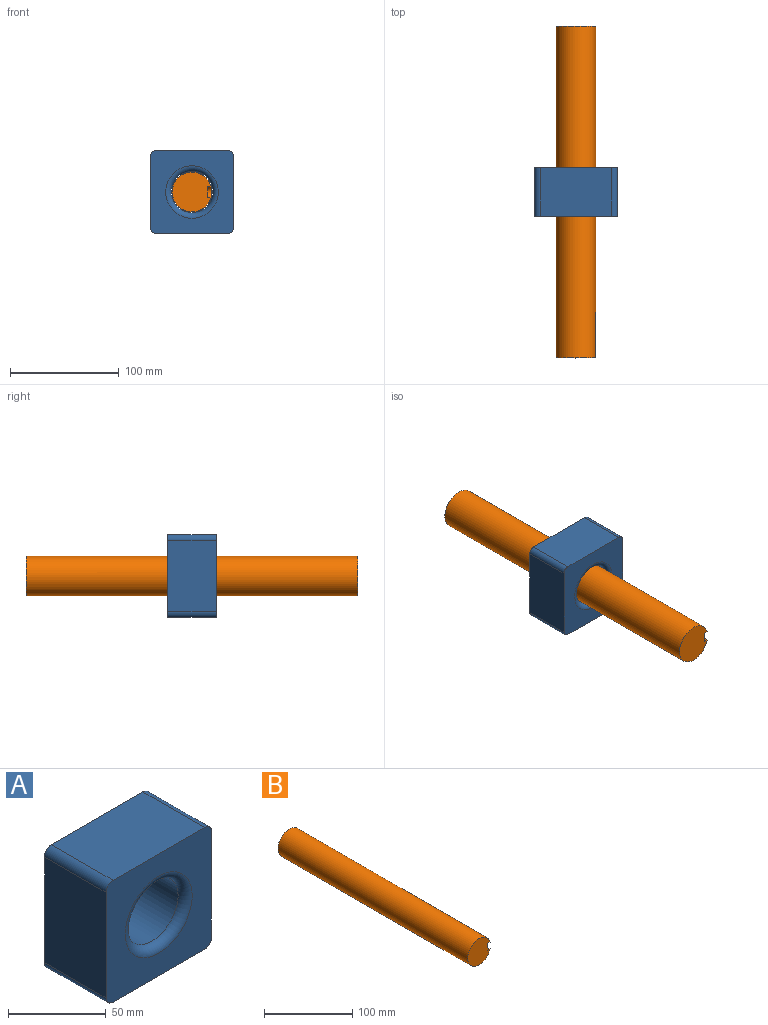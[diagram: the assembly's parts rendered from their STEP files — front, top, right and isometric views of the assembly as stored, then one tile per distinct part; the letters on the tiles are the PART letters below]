
ASSEMBLY  parts=2 mates=2
PART A: 13 faces, bbox 76.2x44.5x76.2 mm
  f0: plane 66.04x44.45mm, normal (0,0,-1), area 2935.5mm2, adj f5,f6,f7,f10
  f1: plane 66.04x44.45mm, normal (1,0,0), area 2935.5mm2, adj f5,f6,f7,f8
  f2: plane 66.04x44.45mm, normal (0,0,1), area 2935.5mm2, adj f5,f6,f8,f9
  f3: cylinder r=19.05mm len=38.1mm, axis (0,1,0), area 4104.3mm2, adj f11,f12
  f4: plane 66.04x44.45mm, normal (-1,0,0), area 2935.5mm2, adj f5,f6,f9,f10
  f5: plane 76.2x76.2mm, normal (0,-1,0), area 3955.1mm2, adj f0,f1,f2,f4,f7,f8,f9,f10
  f6: plane 76.2x76.2mm, normal (0,1,0), area 3955.1mm2, adj f0,f1,f2,f4,f7,f8,f9,f10
  f7: cylinder r=5.08mm len=44.45mm, axis (0,1,0), area 354.7mm2, adj f0,f1,f5,f6
  f8: cylinder r=5.08mm len=44.45mm, axis (0,-1,0), area 354.7mm2, adj f1,f2,f5,f6
  f9: cylinder r=5.08mm len=44.45mm, axis (0,1,0), area 354.7mm2, adj f2,f4,f5,f6
  f10: cylinder r=5.08mm len=44.45mm, axis (0,-1,0), area 354.7mm2, adj f0,f4,f5,f6
  f11: torus R=24.13mm, axis (0,-1,0), area 1047.7mm2, adj f3,f6
  f12: torus R=24.13mm, axis (0,-1,0), area 1047.7mm2, adj f3,f5
PART B: 7 faces, bbox 36.5x304.8x36.5 mm
  f0: cylinder r=18.26mm len=304.8mm, axis (0,1,0), area 34559.7mm2, adj f1,f2,f3,f4,f5
  f1: plane 36.51x35.88mm, normal (0,-1,0), area 1011.3mm2, adj f0,f4,f5,f6
  f2: plane 36.51x36.51mm, normal (0,1,0), area 1047.1mm2, adj f0
  f3: cylinder r=4.76mm len=9.53mm, axis (1,0,0), area 54.7mm2, adj f0,f4,f5,f6
  f4: plane 38.1x3.34mm, normal (0,0,1), area 127.1mm2, adj f0,f1,f3,f6
  f5: plane 38.1x3.34mm, normal (0,0,-1), area 127.1mm2, adj f0,f1,f3,f6
  f6: plane 42.86x9.53mm, normal (1,0,0), area 398.5mm2, adj f1,f3,f4,f5
PLACE A t=(-5.82,-99.99,31.64)mm
PLACE B t=(-5.82,-99.99,31.64)mm
MATE parallel A.f1 <-> B.f6  axis (1,0,0) through (32.28,-99.99,31.64)mm
MATE fastened A.f3 <-> B.f0  axis (0,1,0) through (-5.82,-99.99,31.64)mm
